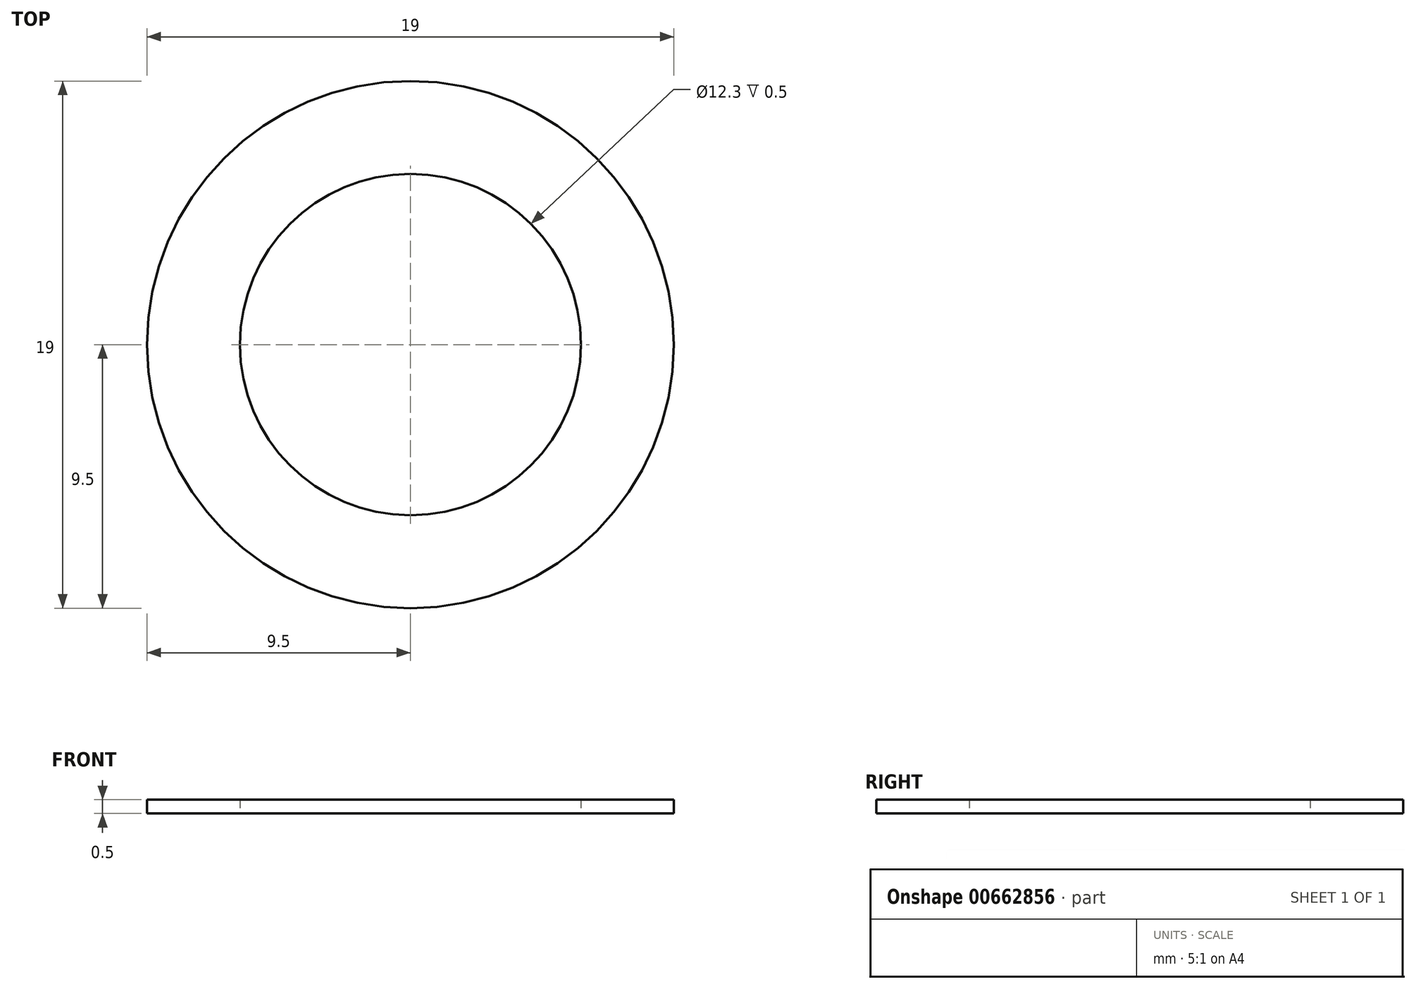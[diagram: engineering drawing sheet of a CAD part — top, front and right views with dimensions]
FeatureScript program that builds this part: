
annotation { "Feature Type Name" : "Feature", "Feature Type Description" : "" }
export const myFeature = defineFeature(function(context is Context, id is Id, definition is map)
    precondition{}
    {
        {
            var Q0;
            Q0=qCreatedBy(makeId("Top.planeOp"),FACE);
            var sketch = newSketch(context, id + "F0", { "sketchPlane" : qUnion([Q0])});
            skCircle(sketch, "E0", {"center": v(0, 0) * mm, "radius": 6.15 * mm});
            skCircle(sketch, "E1.0", {"center": v(0, 0) * mm, "radius": 9.5 * mm});
            skSolve(sketch);
        }
        {
            var Q0;
            Q0=makeQuery(id+"F0.imprint","IMPRINT",FACE,{"disambiguationData":[TD([[makeQuery(id+"F0.imprint","IMPRINT",EDGE,{"derivedFrom":sQuery(id+"F0.wireOp",EDGE,"E0")}),-1.0]])]});
            extrude(context, id + "F1", {"entities" : qUnion([Q0]), "depth" : 0.5 * mm, "offsetDistance" : 25 * mm});
        }
    });
